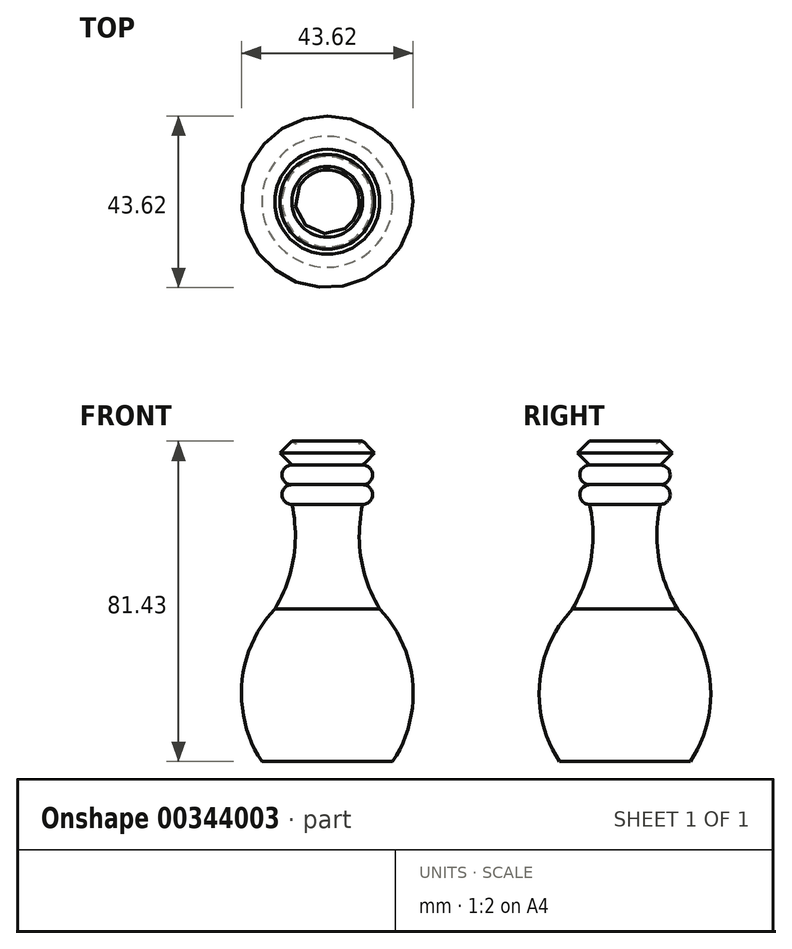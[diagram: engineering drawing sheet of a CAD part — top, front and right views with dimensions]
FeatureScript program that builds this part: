
annotation { "Feature Type Name" : "Feature", "Feature Type Description" : "" }
export const myFeature = defineFeature(function(context is Context, id is Id, definition is map)
    precondition{}
    {
        {
            var Q0;
            Q0=qCreatedBy(makeId("Front.planeOp"),FACE);
            var sketch = newSketch(context, id + "F0", { "sketchPlane" : qUnion([Q0])});
            skLineSegment(sketch, "E0", {"start": v(0, 0) * mm, "end": v(0, -95) * mm});
            skArc(sketch, "E1", {"start": v(9, -29.65) * mm, "mid": v(11.5, -27.15) * mm, "end": v(9, -24.65) * mm});
            skArc(sketch, "E2", {"start": v(9, -24.65) * mm, "mid": v(11.5, -22.15) * mm, "end": v(9, -19.65) * mm});
            skLineSegment(sketch, "E3", {"start": v(9, -19.65) * mm, "end": v(12.04, -16.6) * mm});
            skLineSegment(sketch, "E4", {"start": v(12.04, -16.6) * mm, "end": v(9, -13.57) * mm});
            skArc(sketch, "E5", {"start": v(9, -13.57) * mm, "mid": v(10.78, -2.62) * mm, "end": v(0, 0) * mm});
            skLineSegment(sketch, "E6", {"start": v(0, -95) * mm, "end": v(16.62, -95) * mm});
            skArc(sketch, "E7", {"start": v(16.62, -95) * mm, "mid": v(21.7, -75.03) * mm, "end": v(13.32, -56.2) * mm});
            skArc(sketch, "E8", {"start": v(9, -29.65) * mm, "mid": v(8.59, -43.34) * mm, "end": v(13.32, -56.2) * mm});
            skSolve(sketch);
        }
        {
            var Q0;
            Q0 = qSketchRegion(id + "F0", true);
            var Q1;
            Q1=sQuery(id+"F0.wireOp",EDGE,"E0");
            revolve(context, id + "F1", {"entities" : qUnion([Q0]), "axis" : qUnion([Q1]), "revolveType" : RevolveType.FULL});
        }
    });
